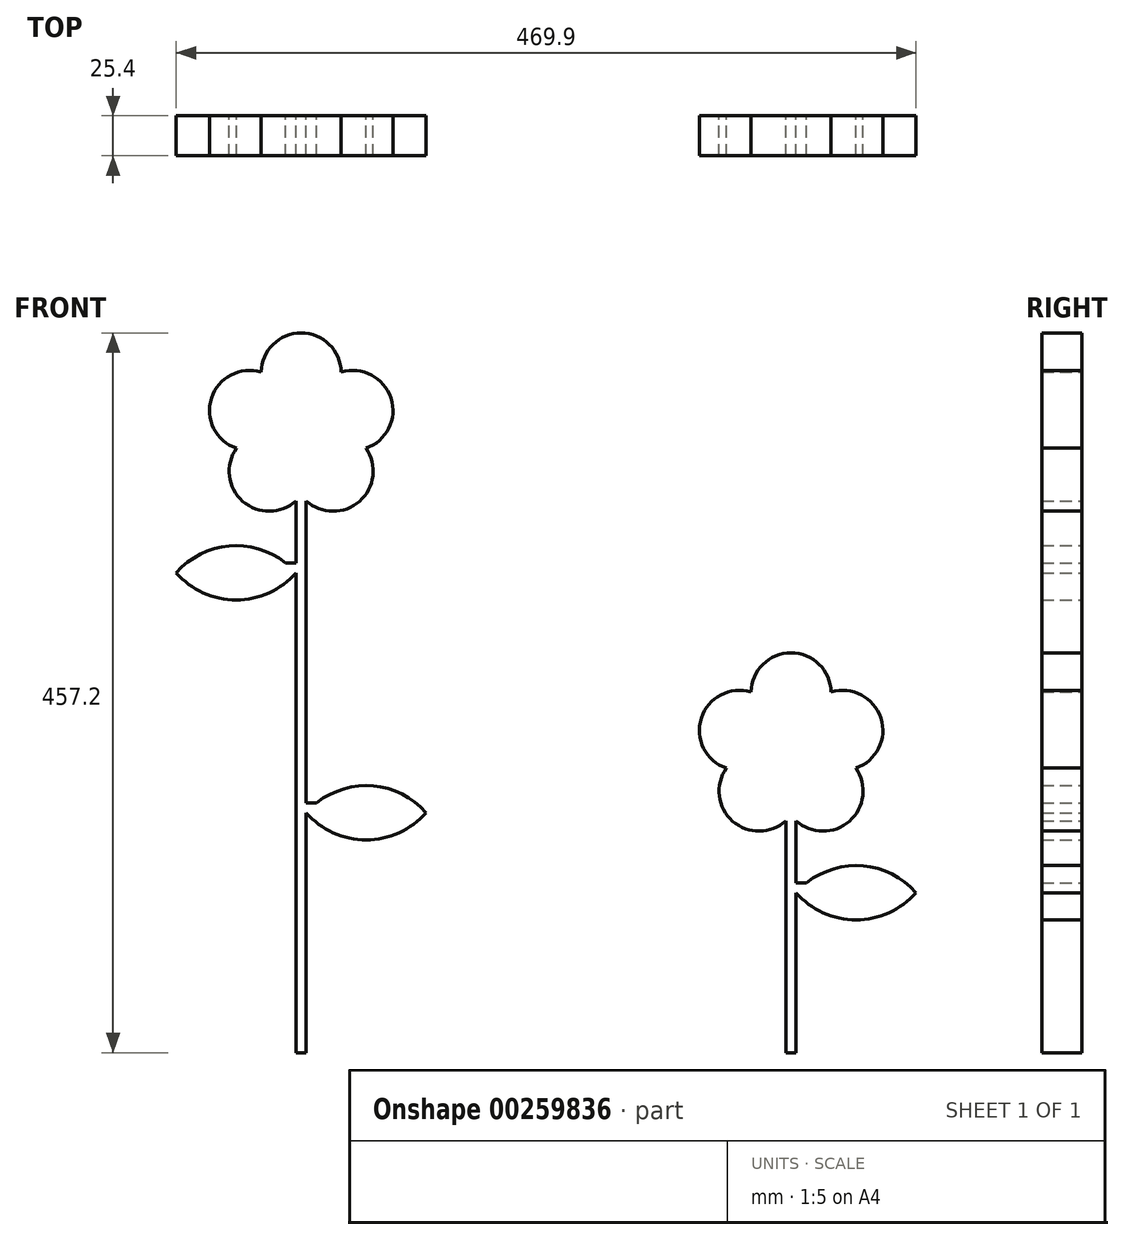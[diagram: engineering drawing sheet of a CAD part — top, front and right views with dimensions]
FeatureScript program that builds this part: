
annotation { "Feature Type Name" : "Feature", "Feature Type Description" : "" }
export const myFeature = defineFeature(function(context is Context, id is Id, definition is map)
    precondition{}
    {
        {
            var Q0;
            Q0=qCreatedBy(makeId("Front.planeOp"),FACE);
            var sketch = newSketch(context, id + "F0", { "sketchPlane" : qUnion([Q0])});
            skLineSegment(sketch, "E0", {"start": v(-6.35, 0) * mm, "end": v(-6.35, 384.95) * mm});
            skLineSegment(sketch, "E1", {"start": v(0, 0) * mm, "end": v(0, 384.95) * mm});
            skCircle(sketch, "E2", {"center": v(-3.18, 397.25) * mm, "radius": 12.7 * mm, "construction": true});
            skPoint(sketch, "E2.third.point", {"position": v(-3.18, 384.55) * mm});
            skLineSegment(sketch, "E3", {"start": v(0, 0) * mm, "end": v(-6.35, 0) * mm});
            skArc(sketch, "E4", {"start": v(-15.25, 393.32) * mm, "mid": v(-38.41, 348.74) * mm, "end": v(-3.17, 384.55) * mm});
            skArc(sketch, "E5", {"start": v(-10.64, 407.52) * mm, "mid": v(-60.2, 415.77) * mm, "end": v(-15.25, 393.32) * mm});
            skArc(sketch, "E6", {"start": v(4.29, 407.52) * mm, "mid": v(-3.17, 457.2) * mm, "end": v(-10.64, 407.52) * mm});
            skArc(sketch, "E7", {"start": v(8.9, 393.32) * mm, "mid": v(53.84, 415.77) * mm, "end": v(4.29, 407.52) * mm});
            skArc(sketch, "E8", {"start": v(-3.17, 384.55) * mm, "mid": v(32.06, 348.74) * mm, "end": v(8.9, 393.32) * mm});
            skLineSegment(sketch, "E9", {"start": v(-3.18, 397.25) * mm, "end": v(-3.18, 384.55) * mm, "construction": true});
            skLineSegment(sketch, "E10", {"start": v(-3.18, 397.25) * mm, "end": v(8.9, 393.32) * mm, "construction": true});
            skLineSegment(sketch, "E11", {"start": v(-3.18, 397.25) * mm, "end": v(4.29, 407.52) * mm, "construction": true});
            skLineSegment(sketch, "E12", {"start": v(-3.18, 397.25) * mm, "end": v(-10.64, 407.52) * mm, "construction": true});
            skLineSegment(sketch, "E13", {"start": v(-3.17, 397.25) * mm, "end": v(-15.25, 393.32) * mm, "construction": true});
            skLineSegment(sketch, "E14", {"start": v(-6.35, 304.8) * mm, "end": v(-82.55, 304.8) * mm, "construction": true});
            skLineSegment(sketch, "E15", {"start": v(0, 152.4) * mm, "end": v(76.2, 152.4) * mm, "construction": true});
            skArc(sketch, "E16", {"start": v(-6.35, 304.8) * mm, "mid": v(-44.45, 322) * mm, "end": v(-82.55, 304.8) * mm});
            skArc(sketch, "E17", {"start": v(-82.55, 304.8) * mm, "mid": v(-44.45, 287.6) * mm, "end": v(-6.35, 304.8) * mm});
            skArc(sketch, "E18", {"start": v(76.2, 152.4) * mm, "mid": v(38.1, 169.6) * mm, "end": v(0, 152.4) * mm});
            skArc(sketch, "E19", {"start": v(0, 152.4) * mm, "mid": v(38.1, 135.2) * mm, "end": v(76.2, 152.4) * mm});
            skLineSegment(sketch, "E20", {"start": v(-6.35, 311.15) * mm, "end": v(-13.07, 311.15) * mm});
            skLineSegment(sketch, "E21", {"start": v(6.72, 158.75) * mm, "end": v(0, 158.75) * mm});
            skLineSegment(sketch, "E22", {"start": v(304.8, 0) * mm, "end": v(304.8, 181.75) * mm});
            skLineSegment(sketch, "E23", {"start": v(311.15, 0) * mm, "end": v(311.15, 181.75) * mm});
            skCircle(sketch, "E24", {"center": v(307.98, 194.05) * mm, "radius": 12.7 * mm, "construction": true});
            skPoint(sketch, "E24.third.point", {"position": v(307.98, 181.35) * mm});
            skLineSegment(sketch, "E25", {"start": v(311.15, 0) * mm, "end": v(304.8, 0) * mm});
            skArc(sketch, "E26", {"start": v(295.9, 190.12) * mm, "mid": v(272.74, 145.54) * mm, "end": v(307.98, 181.35) * mm});
            skArc(sketch, "E27", {"start": v(300.51, 204.32) * mm, "mid": v(250.96, 212.57) * mm, "end": v(295.9, 190.12) * mm});
            skArc(sketch, "E28", {"start": v(315.44, 204.32) * mm, "mid": v(307.98, 254) * mm, "end": v(300.51, 204.32) * mm});
            skArc(sketch, "E29", {"start": v(320.05, 190.12) * mm, "mid": v(365, 212.57) * mm, "end": v(315.44, 204.32) * mm});
            skArc(sketch, "E30", {"start": v(307.98, 181.35) * mm, "mid": v(343.21, 145.54) * mm, "end": v(320.05, 190.12) * mm});
            skLineSegment(sketch, "E31", {"start": v(307.98, 194.05) * mm, "end": v(307.98, 181.35) * mm, "construction": true});
            skLineSegment(sketch, "E32", {"start": v(307.98, 194.05) * mm, "end": v(320.05, 190.12) * mm, "construction": true});
            skLineSegment(sketch, "E33", {"start": v(307.98, 194.05) * mm, "end": v(315.44, 204.32) * mm, "construction": true});
            skLineSegment(sketch, "E34", {"start": v(307.98, 194.05) * mm, "end": v(300.51, 204.32) * mm, "construction": true});
            skLineSegment(sketch, "E35", {"start": v(307.98, 194.05) * mm, "end": v(295.9, 190.12) * mm, "construction": true});
            skLineSegment(sketch, "E36", {"start": v(311.15, 101.6) * mm, "end": v(387.35, 101.6) * mm, "construction": true});
            skArc(sketch, "E37", {"start": v(387.35, 101.6) * mm, "mid": v(349.25, 118.8) * mm, "end": v(311.15, 101.6) * mm});
            skArc(sketch, "E38", {"start": v(311.15, 101.6) * mm, "mid": v(349.25, 84.4) * mm, "end": v(387.35, 101.6) * mm});
            skLineSegment(sketch, "E39", {"start": v(317.87, 107.95) * mm, "end": v(311.15, 107.95) * mm});
            skSolve(sketch);
        }
        {
            var Q0;
            Q0 = qSketchRegion(id + "F0", true);
            var Q1;
            {var subQ0=sQuery(id+"F0.wireOp",EDGE,"E8");var subQ5=sQuery(id+"F0.wireOp",EDGE,"E0");var subQ6=makeQuery(id+"F0.imprint","INTERSECT",VERTEX,{"disambiguationData":[OD(0.0)],"derivedFrom":[subQ5,subQ0]});Q1=makeQuery(id+"F0.imprint","IMPRINT",FACE,{"disambiguationData":[TD([[makeQuery(id+"F0.imprint","IMPRINT",EDGE,{"disambiguationData":[TD([[subQ6,1.0]])],"derivedFrom":subQ5}),-1.0]])]});}
            var Q2;
            {var subQ0=sQuery(id+"F0.wireOp",EDGE,"E8");var subQ1=sQuery(id+"F0.wireOp",EDGE,"E0");var subQ2=makeQuery(id+"F0.imprint","INTERSECT",VERTEX,{"disambiguationData":[OD(0.0)],"derivedFrom":[subQ1,subQ0]});Q2=makeQuery(id+"F0.imprint","IMPRINT",FACE,{"disambiguationData":[TD([[makeQuery(id+"F0.imprint","IMPRINT",EDGE,{"disambiguationData":[TD([[subQ2,1.0]])],"derivedFrom":subQ1}),1.0]])]});}
            var Q3;
            {var subQ0=sQuery(id+"F0.wireOp",EDGE,"E4");var subQ1=sQuery(id+"F0.wireOp",EDGE,"E1");var subQ2=makeQuery(id+"F0.imprint","INTERSECT",VERTEX,{"disambiguationData":[OD(0.0)],"derivedFrom":[subQ1,subQ0]});Q3=makeQuery(id+"F0.imprint","IMPRINT",FACE,{"disambiguationData":[TD([[makeQuery(id+"F0.imprint","IMPRINT",EDGE,{"disambiguationData":[TD([[subQ2,1.0]])],"derivedFrom":subQ1}),-1.0]])]});}
            var Q4;
            {var subQ0=sQuery(id+"F0.wireOp",EDGE,"E30");var subQ7=sQuery(id+"F0.wireOp",EDGE,"E22");var subQ8=makeQuery(id+"F0.imprint","INTERSECT",VERTEX,{"disambiguationData":[OD(0.0)],"derivedFrom":[subQ7,subQ0]});Q4=makeQuery(id+"F0.imprint","IMPRINT",FACE,{"disambiguationData":[TD([[makeQuery(id+"F0.imprint","IMPRINT",EDGE,{"disambiguationData":[TD([[subQ8,1.0]])],"derivedFrom":subQ7}),-1.0]])]});}
            var Q5;
            {var subQ0=sQuery(id+"F0.wireOp",EDGE,"E30");var subQ1=sQuery(id+"F0.wireOp",EDGE,"E22");var subQ2=makeQuery(id+"F0.imprint","INTERSECT",VERTEX,{"disambiguationData":[OD(0.0)],"derivedFrom":[subQ1,subQ0]});Q5=makeQuery(id+"F0.imprint","IMPRINT",FACE,{"disambiguationData":[TD([[makeQuery(id+"F0.imprint","IMPRINT",EDGE,{"disambiguationData":[TD([[subQ2,1.0]])],"derivedFrom":subQ1}),1.0]])]});}
            var Q6;
            {var subQ0=sQuery(id+"F0.wireOp",EDGE,"E26");var subQ1=sQuery(id+"F0.wireOp",EDGE,"E23");var subQ2=makeQuery(id+"F0.imprint","INTERSECT",VERTEX,{"disambiguationData":[OD(0.0)],"derivedFrom":[subQ1,subQ0]});Q6=makeQuery(id+"F0.imprint","IMPRINT",FACE,{"disambiguationData":[TD([[makeQuery(id+"F0.imprint","IMPRINT",EDGE,{"disambiguationData":[TD([[subQ2,1.0]])],"derivedFrom":subQ1}),-1.0]])]});}
            extrude(context, id + "F1", {"entities" : qUnion([Q0, Q1, Q2, Q3, Q4, Q5, Q6]), "depth" : 25.4 * mm});
        }
    });
